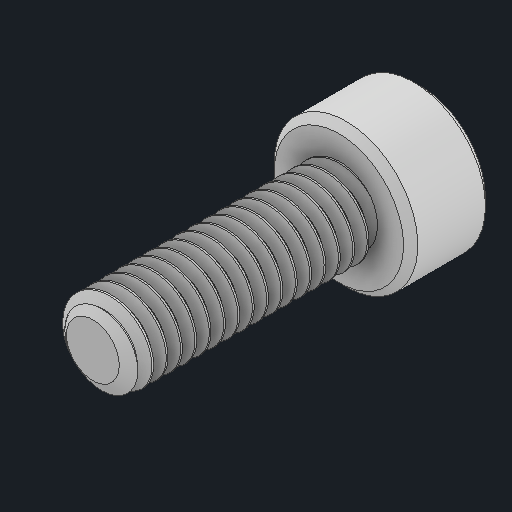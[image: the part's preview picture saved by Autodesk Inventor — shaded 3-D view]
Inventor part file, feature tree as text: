
AUTODESK INVENTOR PART (.ipt)
format: ipt  version: 2024 (Build 280153000, 153)  size: 609,280 bytes
history: native  units: in
note: dims shown in document units (in); Inventor stores cm internally (conversion verified against a paired STEP export)
features: chamfer x1
ambient origin geometry x8: Origin, YZ Plane, XZ Plane, XY Plane, X Axis, Y Axis, Z Axis, Center Point
bodies: Solid1 (feature_tree)
feature tree (1):
  chamfer  "Chamfer1"  [1 undecoded]
note: 1 required parameter value undecoded (feature->parameter linkage not recoverable at this tier; creation-order binding heuristic only, values carry confidence <= 0.55)
